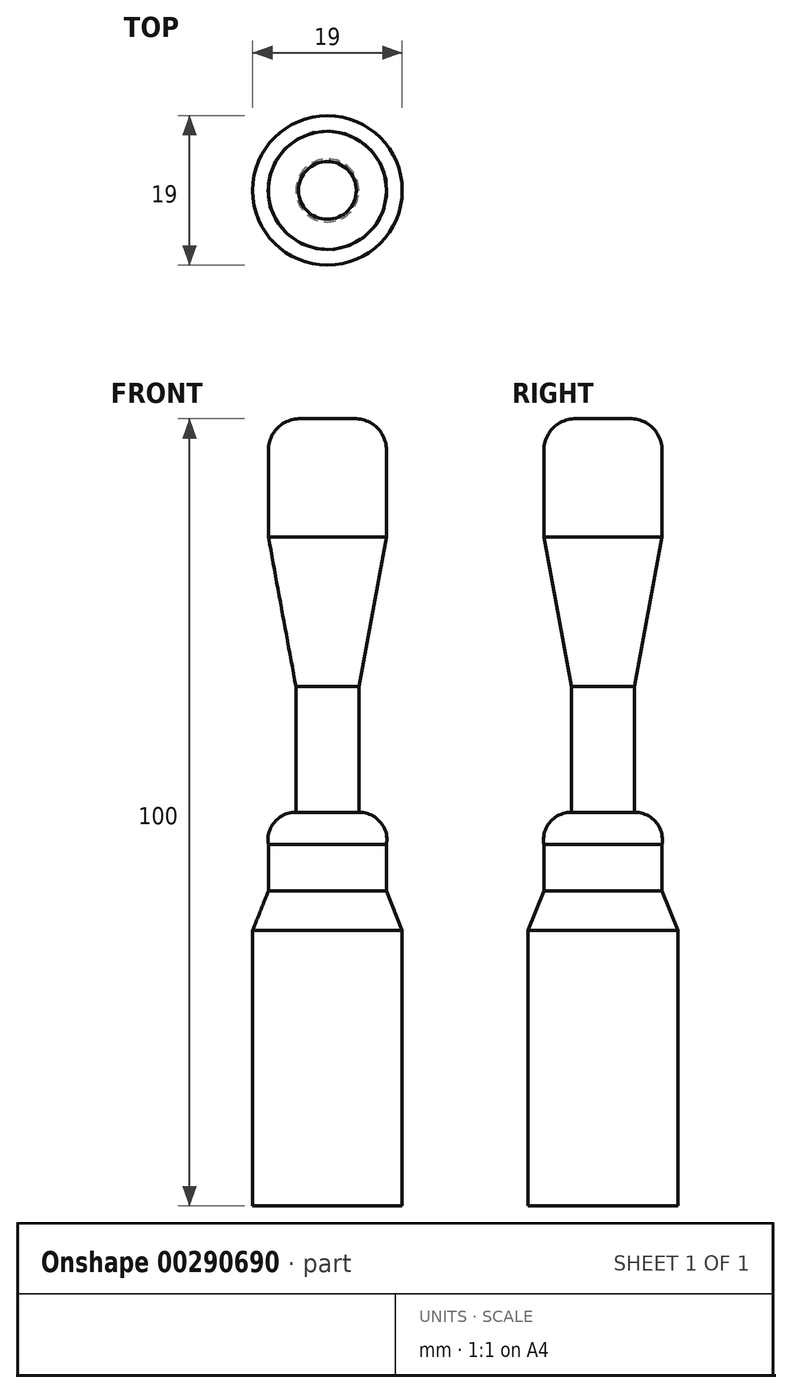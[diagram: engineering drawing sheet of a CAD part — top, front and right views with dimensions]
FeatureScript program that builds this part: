
annotation { "Feature Type Name" : "Feature", "Feature Type Description" : "" }
export const myFeature = defineFeature(function(context is Context, id is Id, definition is map)
    precondition{}
    {
        {
            var Q0;
            Q0=qCreatedBy(makeId("Front.planeOp"),FACE);
            var sketch = newSketch(context, id + "F0", { "sketchPlane" : qUnion([Q0])});
            skLineSegment(sketch, "E0", {"start": v(0, 0) * mm, "end": v(3.67, 0) * mm});
            skLineSegment(sketch, "E1", {"start": v(7.5, -4) * mm, "end": v(7.5, -15) * mm});
            skLineSegment(sketch, "E2", {"start": v(7.5, -15) * mm, "end": v(4, -34) * mm});
            skLineSegment(sketch, "E3", {"start": v(4, -34) * mm, "end": v(4, -50) * mm});
            skLineSegment(sketch, "E4", {"start": v(7.5, -54.1) * mm, "end": v(7.5, -60) * mm});
            skLineSegment(sketch, "E5", {"start": v(7.5, -60) * mm, "end": v(9.5, -65) * mm});
            skLineSegment(sketch, "E6", {"start": v(9.5, -65) * mm, "end": v(9.5, -100) * mm});
            skLineSegment(sketch, "E7", {"start": v(9.5, -100) * mm, "end": v(0, -100) * mm});
            skLineSegment(sketch, "E8", {"start": v(0, -100) * mm, "end": v(0, 0) * mm});
            skArc(sketch, "E9", {"start": v(7.5, -54.1) * mm, "mid": v(6.7, -51.22) * mm, "end": v(4, -50) * mm});
            skArc(sketch, "E10", {"start": v(7.5, -4) * mm, "mid": v(6.39, -1.23) * mm, "end": v(3.67, 0) * mm});
            skSolve(sketch);
        }
        {
            var Q0;
            Q0 = qSketchRegion(id + "F0", true);
            var Q1;
            Q1=sQuery(id+"F0.wireOp",EDGE,"E8");
            revolve(context, id + "F1", {"entities" : qUnion([Q0]), "axis" : qUnion([Q1]), "revolveType" : RevolveType.FULL});
        }
    });
